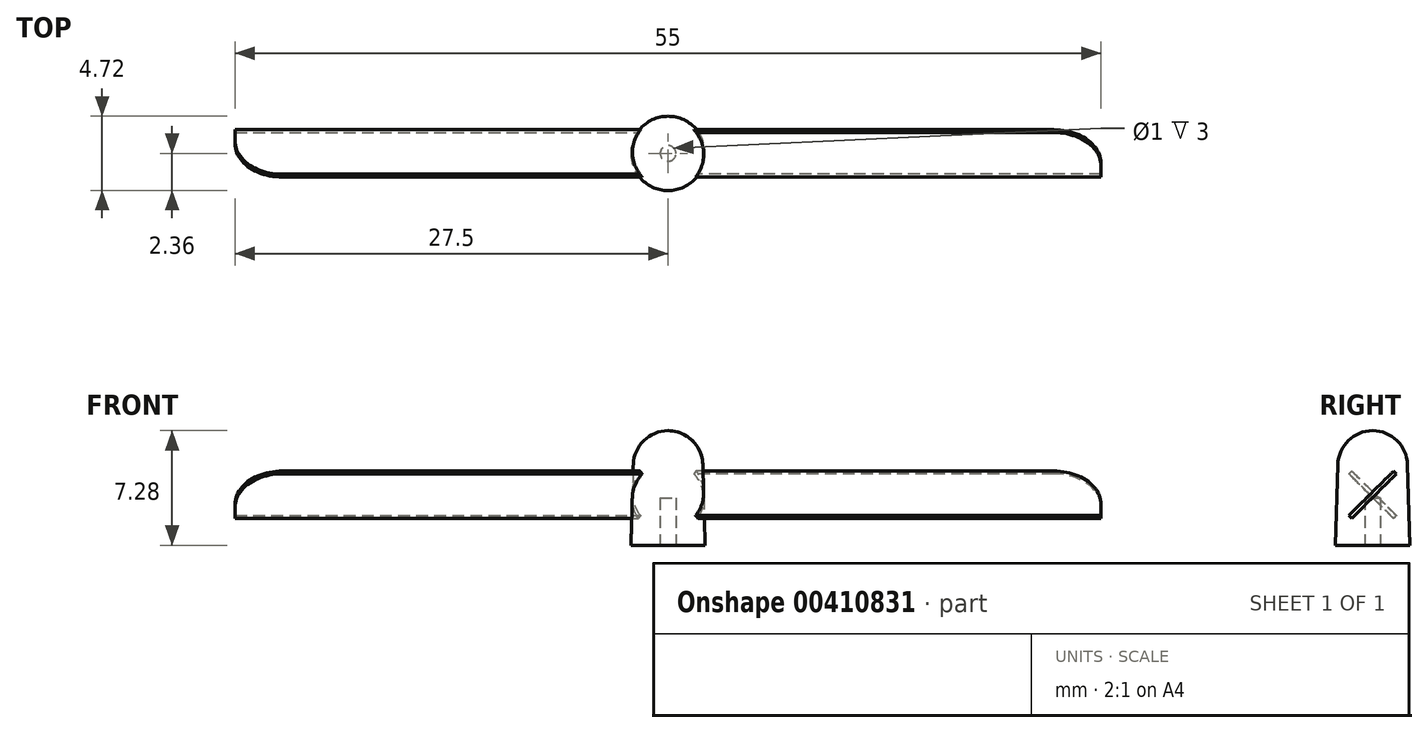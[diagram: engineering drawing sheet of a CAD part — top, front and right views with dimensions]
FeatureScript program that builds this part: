
annotation { "Feature Type Name" : "Feature", "Feature Type Description" : "" }
export const myFeature = defineFeature(function(context is Context, id is Id, definition is map)
    precondition{}
    {
        {
            var Q0;
            Q0=qCreatedBy(makeId("Right.planeOp"),FACE);
            var sketch = newSketch(context, id + "F0", { "sketchPlane" : qUnion([Q0])});
            skLineSegment(sketch, "E0", {"start": v(-1.5, -1.33) * mm, "end": v(-1.33, -1.5) * mm});
            skLineSegment(sketch, "E1", {"start": v(1.33, 1.5) * mm, "end": v(1.5, 1.33) * mm});
            skLineSegment(sketch, "E2", {"start": v(-1.5, -1.33) * mm, "end": v(1.33, 1.5) * mm});
            skLineSegment(sketch, "E3", {"start": v(-1.33, -1.5) * mm, "end": v(1.5, 1.33) * mm});
            skSolve(sketch);
        }
        {
            var Q0;
            Q0 = qSketchRegion(id + "F0", true);
            extrude(context, id + "F1", {"entities" : qUnion([Q0]), "depth" : 27.5 * mm});
        }
        {
            var Q0;
            Q0=makeQuery(id+"F1.opExtrude","CAP_EDGE",EDGE,{"disambiguationData":[OSD([sQuery(id+"F0.wireOp",EDGE,"E1")])],"isStart":false});
            fillet(context, id + "F2", {"entities" : qUnion([Q0]), "radius" : 3 * mm, "tangentPropagation" : true, "allowEdgeOverflow" : false});
        }
        {
            var Q0;
            Q0=qCreatedBy(makeId("Front.planeOp"),FACE);
            var sketch = newSketch(context, id + "F3", { "sketchPlane" : qUnion([Q0])});
            skLineSegment(sketch, "E4", {"start": v(2.2, 1.92) * mm, "end": v(2.36, -3.21) * mm});
            skLineSegment(sketch, "E5", {"start": v(2.36, -3.21) * mm, "end": v(0, -3.21) * mm});
            skLineSegment(sketch, "E6", {"start": v(0, -3.21) * mm, "end": v(0, 4.07) * mm});
            skPoint(sketch, "E7.orphan", {"position": v(2.27, 0) * mm});
            skArc(sketch, "E8", {"start": v(2.2, 1.92) * mm, "mid": v(1.54, 3.44) * mm, "end": v(0, 4.07) * mm});
            skSolve(sketch);
        }
        {
            var Q0;
            Q0 = qSketchRegion(id + "F3", true);
            var Q1;
            Q1=sQuery(id+"F3.wireOp",EDGE,"E6");
            revolve(context, id + "F4", {"operationType" : NewBodyOperationType.ADD, "entities" : qUnion([Q0]), "axis" : qUnion([Q1]), "revolveType" : RevolveType.FULL});
        }
        {
            var Q0;
            Q0=makeQuery(id+"F1.opExtrude","SWEPT_BODY",BODY,{"disambiguationData":[OSD([sQuery(id+"F0.wireOp",EDGE,"E0"),sQuery(id+"F0.wireOp",EDGE,"E1"),sQuery(id+"F0.wireOp",EDGE,"E2"),sQuery(id+"F0.wireOp",EDGE,"E3")])]});
            var Q1;
            Q1=makeQuery(id+"F4.opRevolve","SWEPT_EDGE",EDGE,{"disambiguationData":[OSD([sQuery(id+"F3.wireOp",EDGE,"E4"),sQuery(id+"F3.wireOp",EDGE,"E5")])]});
            circularPattern(context, id + "F5", {"operationType" : NewBodyOperationType.ADD, "entities" : qUnion([Q0]), "axis" : qUnion([Q1]), "angle" : 360 * degree, "instanceCount" : 2, "equalSpace" : true});
        }
        {
            var Q0;
            Q0=makeQuery(id+"F4.opRevolve","SWEPT_FACE",FACE,{"disambiguationData":[OSD([sQuery(id+"F3.wireOp",EDGE,"E5")])]});
            var sketch = newSketch(context, id + "F6", { "sketchPlane" : qUnion([Q0])});
            skCircle(sketch, "E9", {"center": v(0, 0) * mm, "radius": 0.5 * mm});
            skSolve(sketch);
        }
        {
            var Q0;
            Q0 = qSketchRegion(id + "F6", true);
            extrude(context, id + "F7", {"entities" : qUnion([Q0]), "operationType" : NewBodyOperationType.REMOVE, "oppositeDirection" : true, "depth" : 3 * mm});
        }
    });
